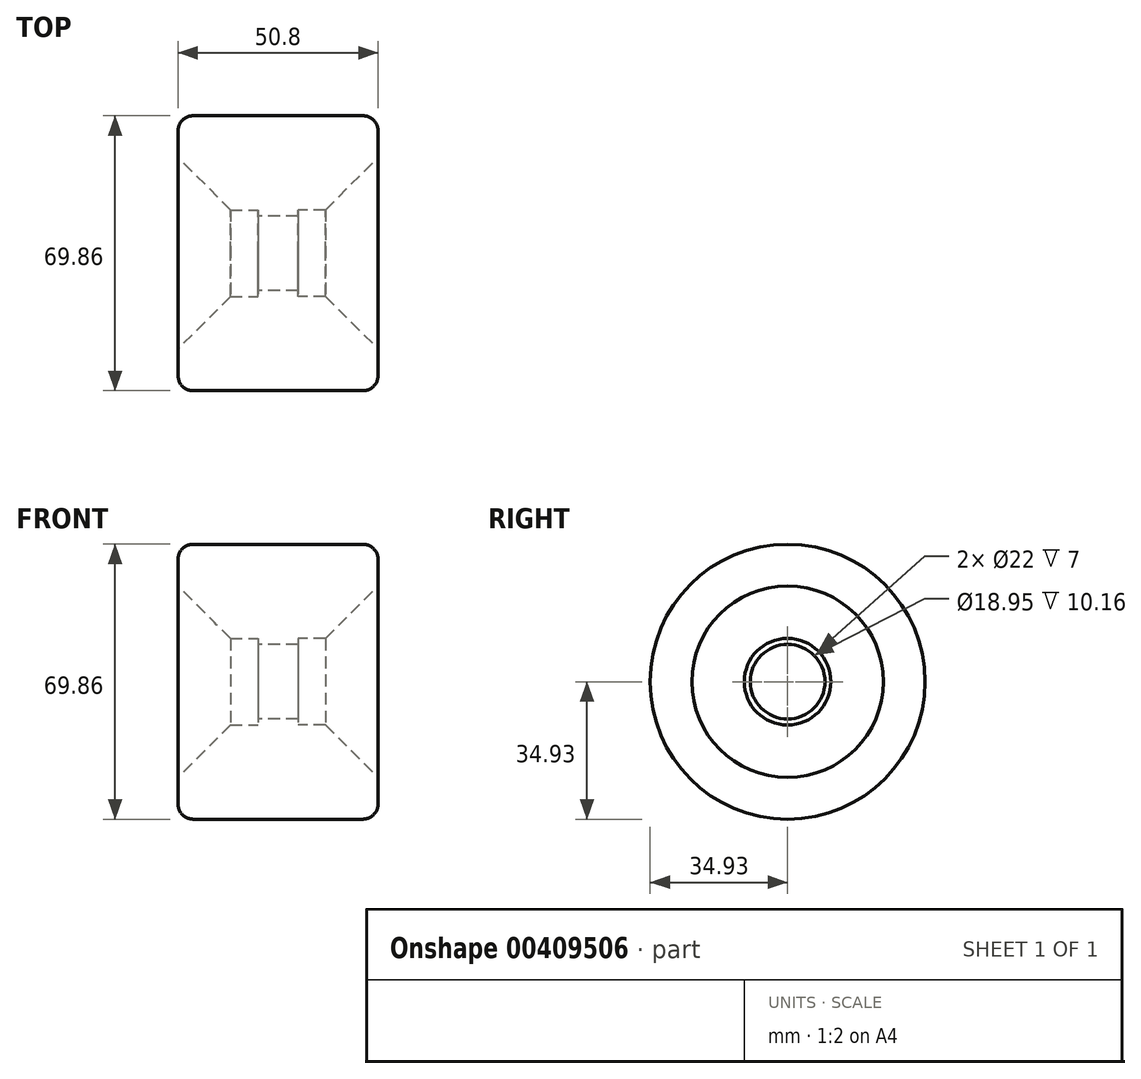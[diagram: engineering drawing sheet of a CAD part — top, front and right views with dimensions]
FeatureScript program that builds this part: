
annotation { "Feature Type Name" : "Feature", "Feature Type Description" : "" }
export const myFeature = defineFeature(function(context is Context, id is Id, definition is map)
    precondition{}
    {
        {
            var Q0;
            Q0=qCreatedBy(makeId("Front.planeOp"),FACE);
            var sketch = newSketch(context, id + "F0", { "sketchPlane" : qUnion([Q0])});
            skLineSegment(sketch, "E0", {"start": v(0, 9.48) * mm, "end": v(0, 34.93) * mm});
            skLineSegment(sketch, "E1", {"start": v(25.4, 31.12) * mm, "end": v(25.4, 24.32) * mm});
            skLineSegment(sketch, "E2", {"start": v(25.4, 24.32) * mm, "end": v(12.08, 11) * mm});
            skLineSegment(sketch, "E3", {"start": v(12.08, 11) * mm, "end": v(5.08, 11) * mm});
            skLineSegment(sketch, "E4", {"start": v(5.08, 11) * mm, "end": v(5.08, 9.48) * mm});
            skLineSegment(sketch, "E5", {"start": v(5.08, 9.48) * mm, "end": v(0, 9.48) * mm});
            skLineSegment(sketch, "E6", {"start": v(0, 34.93) * mm, "end": v(21.59, 34.93) * mm});
            skLineSegment(sketch, "E7", {"start": v(0, 0) * mm, "end": v(0, 9.48) * mm, "construction": true});
            skLineSegment(sketch, "E8", {"start": v(0, 0) * mm, "end": v(34.98, 0) * mm, "construction": true});
            skPoint(sketch, "E9.visualSharp", {"position": v(25.4, 34.93) * mm});
            skArc(sketch, "E9.filletArc", {"start": v(25.4, 31.12) * mm, "mid": v(24.28, 33.8) * mm, "end": v(21.59, 34.92) * mm});
            skSolve(sketch);
        }
        {
            var Q0;
            Q0 = qSketchRegion(id + "F0", true);
            var Q1;
            Q1=sQuery(id+"F0.wireOp",EDGE,"E8");
            revolve(context, id + "F1", {"entities" : qUnion([Q0]), "axis" : qUnion([Q1]), "revolveType" : RevolveType.FULL});
        }
        {
            var Q0;
            Q0=makeQuery(id+"F1.opRevolve","SWEPT_BODY",BODY,{"disambiguationData":[OSD([sQuery(id+"F0.wireOp",EDGE,"E0"),sQuery(id+"F0.wireOp",EDGE,"E1"),sQuery(id+"F0.wireOp",EDGE,"E2"),sQuery(id+"F0.wireOp",EDGE,"E3"),sQuery(id+"F0.wireOp",EDGE,"E4"),sQuery(id+"F0.wireOp",EDGE,"E5"),sQuery(id+"F0.wireOp",EDGE,"E6"),sQuery(id+"F0.wireOp",EDGE,"E9.filletArc")])]});
            var Q1;
            Q1=makeQuery(id+"F1.opRevolve","SWEPT_FACE",FACE,{"disambiguationData":[OSD([sQuery(id+"F0.wireOp",EDGE,"E0")])]});
            mirror(context, id + "F2", {"operationType" : NewBodyOperationType.ADD, "entities" : qUnion([Q0]), "mirrorPlane" : qUnion([Q1])});
        }
    });
